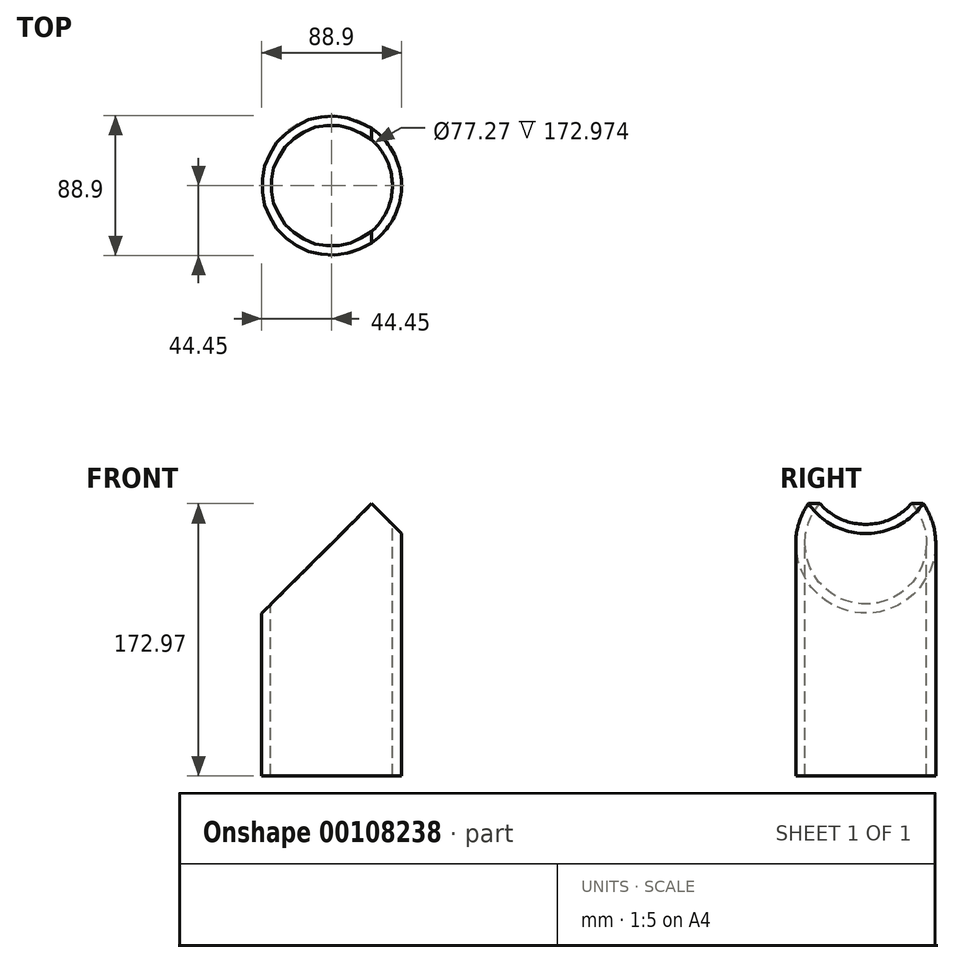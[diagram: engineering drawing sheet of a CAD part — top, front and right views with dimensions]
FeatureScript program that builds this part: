
annotation { "Feature Type Name" : "Feature", "Feature Type Description" : "" }
export const myFeature = defineFeature(function(context is Context, id is Id, definition is map)
    precondition{}
    {
        {
            var Q0;
            Q0=qCreatedBy(makeId("Front.planeOp"),FACE);
            var sketch = newSketch(context, id + "F0", { "sketchPlane" : qUnion([Q0])});
            skLineSegment(sketch, "E0", {"start": v(0, 190.5) * mm, "end": v(0, -190.5) * mm, "construction": true});
            skLineSegment(sketch, "E1", {"start": v(38.63, -96.01) * mm, "end": v(38.63, 96.01) * mm});
            skLineSegment(sketch, "E2", {"start": v(44.45, 96.01) * mm, "end": v(44.45, -96.01) * mm});
            skPoint(sketch, "E3", {"position": v(38.63, 0) * mm});
            skLineSegment(sketch, "E4", {"start": v(38.63, 96.01) * mm, "end": v(44.45, 96.01) * mm});
            skLineSegment(sketch, "E5", {"start": v(38.63, -96.01) * mm, "end": v(44.45, -96.01) * mm});
            skSolve(sketch);
        }
        {
            var Q0;
            Q0=makeQuery(id+"F0.imprint","IMPRINT",FACE,{"disambiguationData":[TD([[makeQuery(id+"F0.imprint","IMPRINT",EDGE,{"derivedFrom":sQuery(id+"F0.wireOp",EDGE,"E1")}),-1.0]])]});
            var Q1;
            Q1=sQuery(id+"F0.wireOp",EDGE,"E0");
            revolve(context, id + "F1", {"entities" : qUnion([Q0]), "axis" : qUnion([Q1]), "revolveType" : RevolveType.FULL});
        }
        {
            var Q0;
            Q0=qCreatedBy(makeId("Front.planeOp"),FACE);
            var sketch = newSketch(context, id + "F2", { "sketchPlane" : qUnion([Q0])});
            skLineSegment(sketch, "E6", {"start": v(25.4, 76.96) * mm, "end": v(-44.45, 7.11) * mm});
            skLineSegment(sketch, "E7", {"start": v(-44.45, 7.11) * mm, "end": v(-44.45, 96.01) * mm});
            skLineSegment(sketch, "E8", {"start": v(-44.45, 96.01) * mm, "end": v(44.45, 96.01) * mm});
            skLineSegment(sketch, "E9", {"start": v(44.45, 96.01) * mm, "end": v(44.45, 0) * mm, "construction": true});
            skLineSegment(sketch, "E10", {"start": v(-44.45, 96.01) * mm, "end": v(-44.45, 0) * mm, "construction": true});
            skPoint(sketch, "E11", {"position": v(0, 96.01) * mm});
            skLineSegment(sketch, "E12", {"start": v(44.45, 96.01) * mm, "end": v(44.45, 96.01) * mm});
            skLineSegment(sketch, "E13", {"start": v(25.4, 76.96) * mm, "end": v(44.45, 76.96) * mm, "construction": true});
            skLineSegment(sketch, "E14", {"start": v(44.45, 76.96) * mm, "end": v(44.45, 96.01) * mm});
            skLineSegment(sketch, "E15", {"start": v(25.4, 76.96) * mm, "end": v(44.45, 57.91) * mm});
            skLineSegment(sketch, "E16", {"start": v(44.45, 76.96) * mm, "end": v(44.45, 57.91) * mm});
            skSolve(sketch);
        }
        {
            var Q0;
            Q0 = qSketchRegion(id + "F2", true);
            extrude(context, id + "F3", {"entities" : qUnion([Q0]), "operationType" : NewBodyOperationType.REMOVE, "endBound" : BoundingType.SYMMETRIC, "oppositeDirection" : true, "depth" : 88.9 * mm});
        }
    });
